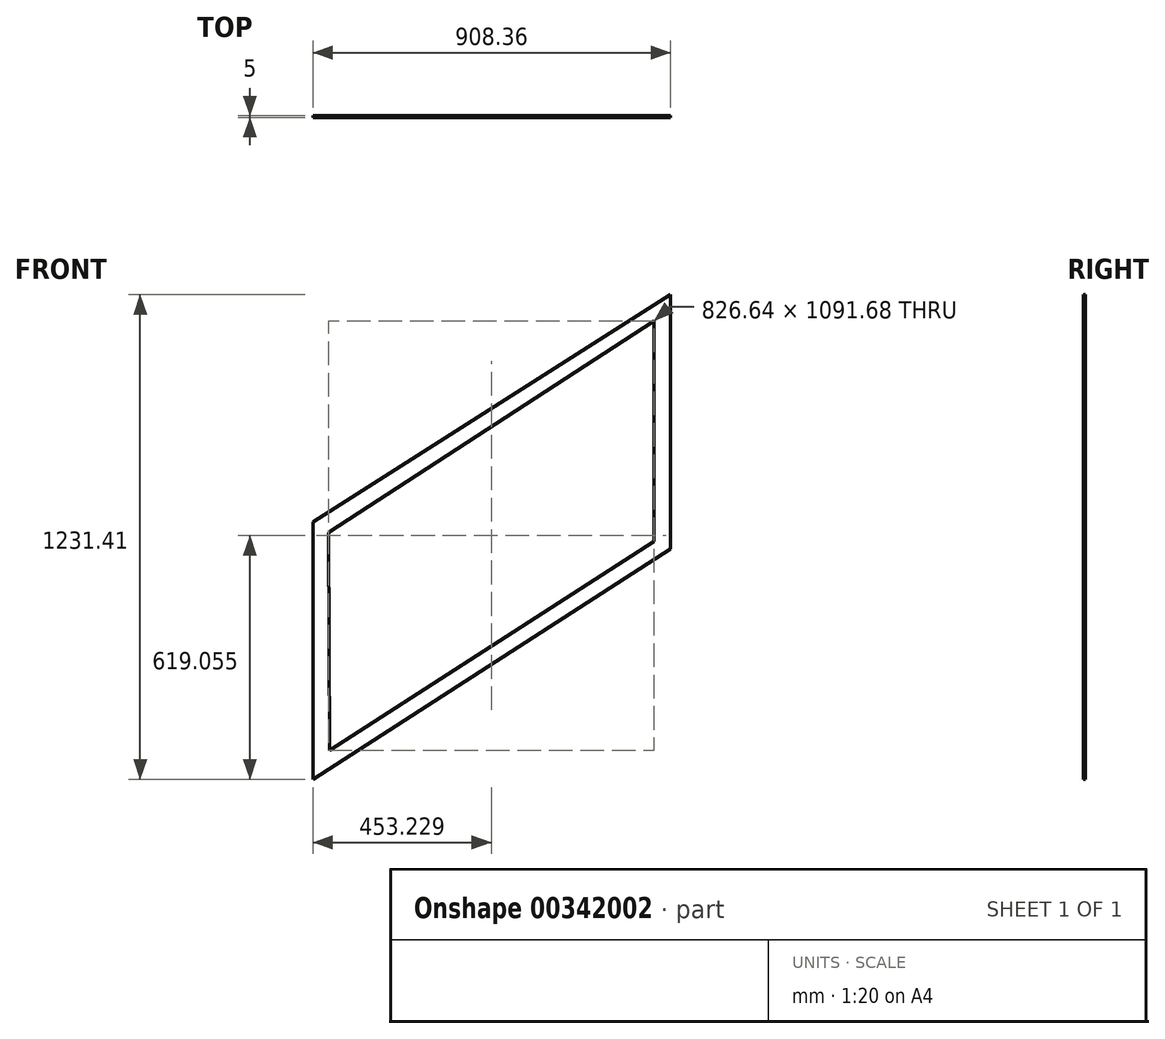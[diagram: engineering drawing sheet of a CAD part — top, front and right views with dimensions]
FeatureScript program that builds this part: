
annotation { "Feature Type Name" : "Feature", "Feature Type Description" : "" }
export const myFeature = defineFeature(function(context is Context, id is Id, definition is map)
    precondition{}
    {
        {
            var Q0;
            Q0=qCreatedBy(makeId("Front.planeOp"),FACE);
            var sketch = newSketch(context, id + "F0", { "sketchPlane" : qUnion([Q0])});
            skLineSegment(sketch, "E0", {"start": v(44.03, 800.1) * mm, "end": v(44.03, 146.39) * mm});
            skLineSegment(sketch, "E1", {"start": v(44.03, 146.39) * mm, "end": v(952.39, 731.81) * mm});
            skLineSegment(sketch, "E2", {"start": v(952.39, 731.81) * mm, "end": v(952.39, 1377.8) * mm});
            skLineSegment(sketch, "E3", {"start": v(952.39, 1377.8) * mm, "end": v(44.03, 800.1) * mm});
            skLineSegment(sketch, "E4", {"start": v(83.94, 773.5) * mm, "end": v(910.58, 1311.28) * mm});
            skLineSegment(sketch, "E5", {"start": v(910.58, 1311.28) * mm, "end": v(910.58, 750.69) * mm});
            skLineSegment(sketch, "E6", {"start": v(910.58, 750.69) * mm, "end": v(86.54, 219.6) * mm});
            skLineSegment(sketch, "E7", {"start": v(86.54, 219.6) * mm, "end": v(83.94, 773.5) * mm});
            skSolve(sketch);
        }
        {
            var Q0;
            Q0 = qSketchRegion(id + "F0", true);
            extrude(context, id + "F1", {"entities" : qUnion([Q0]), "depth" : 5 * mm});
        }
    });
